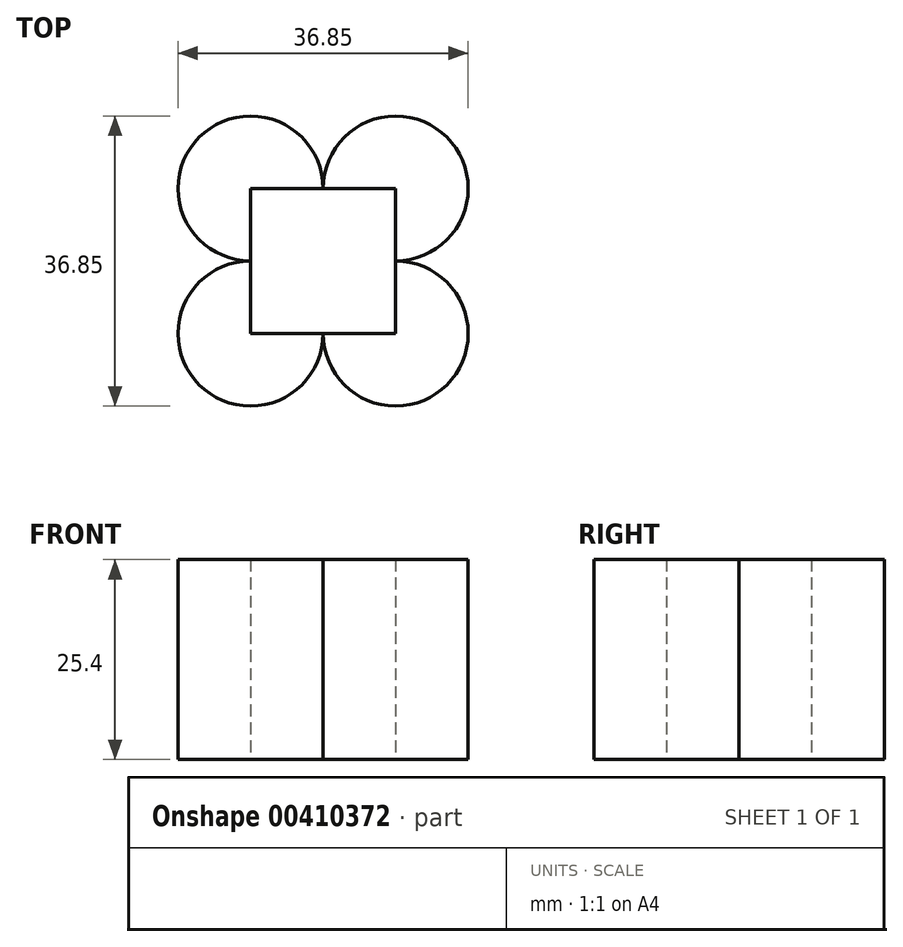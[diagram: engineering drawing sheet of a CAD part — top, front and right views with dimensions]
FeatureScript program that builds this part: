
annotation { "Feature Type Name" : "Feature", "Feature Type Description" : "" }
export const myFeature = defineFeature(function(context is Context, id is Id, definition is map)
    precondition{}
    {
        {
            var Q0;
            Q0=qCreatedBy(makeId("Top.planeOp"),FACE);
            var sketch = newSketch(context, id + "F0", { "sketchPlane" : qUnion([Q0])});
            skLineSegment(sketch, "E0.bottom", {"start": v(-37.5, 74.49) * mm, "end": v(-19.08, 74.49) * mm});
            skLineSegment(sketch, "E0.top", {"start": v(-37.5, 92.91) * mm, "end": v(-19.08, 92.91) * mm});
            skLineSegment(sketch, "E0.left", {"start": v(-37.5, 74.49) * mm, "end": v(-37.5, 92.91) * mm});
            skLineSegment(sketch, "E0.right", {"start": v(-19.08, 74.49) * mm, "end": v(-19.08, 92.91) * mm});
            skCircle(sketch, "E1", {"center": v(-19.08, 74.49) * mm, "radius": 9.21 * mm});
            skCircle(sketch, "E2", {"center": v(-37.5, 74.49) * mm, "radius": 9.21 * mm});
            skCircle(sketch, "E3", {"center": v(-37.5, 92.91) * mm, "radius": 9.21 * mm});
            skCircle(sketch, "E4", {"center": v(-19.08, 92.91) * mm, "radius": 9.21 * mm});
            skSolve(sketch);
        }
        {
            var Q0;
            {var subQ0=sQuery(id+"F0.wireOp",EDGE,"E0.left");var subQ1=sQuery(id+"F0.wireOp",EDGE,"E0.top");var subQ2=makeQuery(id+"F0.imprint","INTERSECT",VERTEX,{"derivedFrom":[subQ1,subQ0]});Q0=makeQuery(id+"F0.imprint","IMPRINT",FACE,{"disambiguationData":[TD([[makeQuery(id+"F0.imprint","IMPRINT",EDGE,{"disambiguationData":[TD([[subQ2,-1.0]])],"derivedFrom":subQ1}),1.0]])]});}
            var Q1;
            {var subQ0=sQuery(id+"F0.wireOp",EDGE,"E0.right");var subQ1=sQuery(id+"F0.wireOp",EDGE,"E0.top");var subQ2=makeQuery(id+"F0.imprint","INTERSECT",VERTEX,{"derivedFrom":[subQ1,subQ0]});Q1=makeQuery(id+"F0.imprint","IMPRINT",FACE,{"disambiguationData":[TD([[makeQuery(id+"F0.imprint","IMPRINT",EDGE,{"disambiguationData":[TD([[subQ2,1.0]])],"derivedFrom":subQ1}),1.0]])]});}
            var Q2;
            {var subQ0=sQuery(id+"F0.wireOp",EDGE,"E0.right");var subQ1=sQuery(id+"F0.wireOp",EDGE,"E0.bottom");var subQ2=makeQuery(id+"F0.imprint","INTERSECT",VERTEX,{"derivedFrom":[subQ1,subQ0]});Q2=makeQuery(id+"F0.imprint","IMPRINT",FACE,{"disambiguationData":[TD([[makeQuery(id+"F0.imprint","IMPRINT",EDGE,{"disambiguationData":[TD([[subQ2,1.0]])],"derivedFrom":subQ1}),-1.0]])]});}
            var Q3;
            {var subQ0=sQuery(id+"F0.wireOp",EDGE,"E0.left");var subQ1=sQuery(id+"F0.wireOp",EDGE,"E0.bottom");var subQ2=makeQuery(id+"F0.imprint","INTERSECT",VERTEX,{"derivedFrom":[subQ1,subQ0]});Q3=makeQuery(id+"F0.imprint","IMPRINT",FACE,{"disambiguationData":[TD([[makeQuery(id+"F0.imprint","IMPRINT",EDGE,{"disambiguationData":[TD([[subQ2,-1.0]])],"derivedFrom":subQ1}),-1.0]])]});}
            extrude(context, id + "F1", {"entities" : qUnion([Q0, Q1, Q2, Q3]), "depth" : 25.4 * mm});
        }
    });
